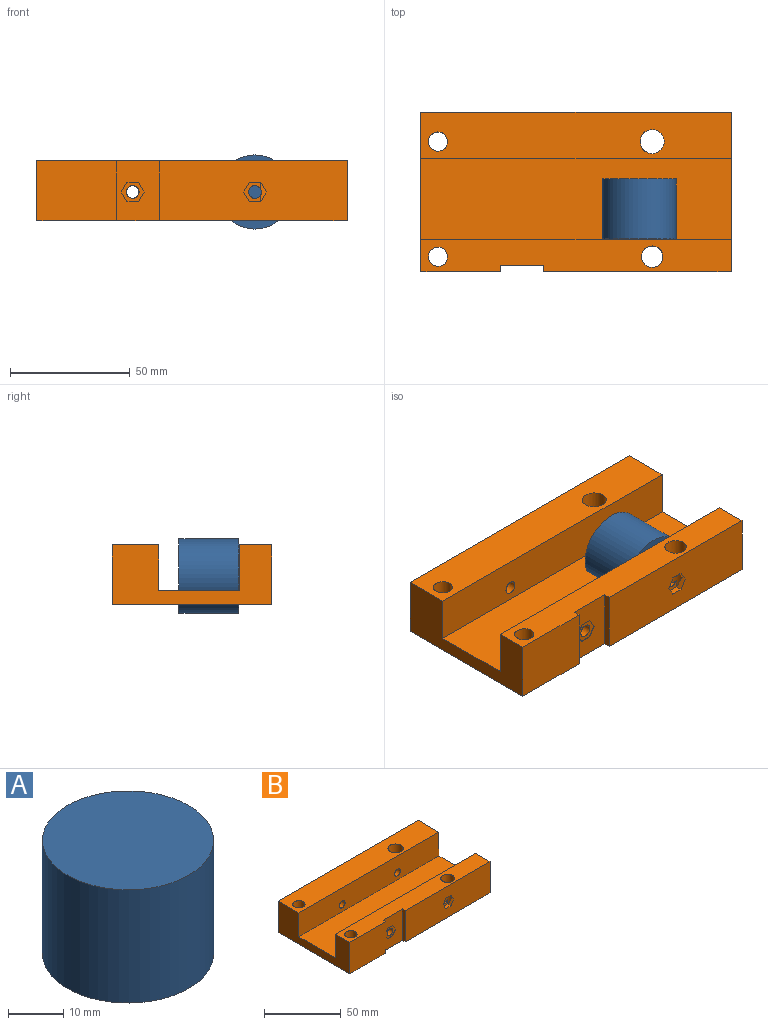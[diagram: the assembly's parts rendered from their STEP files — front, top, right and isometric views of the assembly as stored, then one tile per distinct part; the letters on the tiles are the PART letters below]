
ASSEMBLY  parts=2 mates=1
PART A: 3 faces, bbox 30.9x30.9x25 mm
  f0: cylinder r=15.45mm len=30.9mm, axis (0,0,-1), area 2426.6mm2, adj f1,f2
  f1: plane 30.9x30.9mm, normal (0,0,1), area 749.7mm2, adj f0
  f2: plane 30.9x30.9mm, normal (0,0,-1), area 749.7mm2, adj f0
PART B: 36 faces, bbox 129.2x66.4x25 mm
  f0: cylinder r=2.65mm len=10.43mm, axis (0,-1,0), area 138.4mm2, adj f1,f16,f35
  f1: plane 8.31x7.22mm, normal (0,-1,0), area 28.3mm2, adj f0,f21,f22,f23,f24,f25,f26,f35
  f2: cylinder r=5mm len=25mm, axis (0,0,-1), area 742.5mm2, adj f8,f9,f10
  f3: plane 129.24x25mm, normal (0,1,0), area 3187mm2, adj f4,f7,f8,f9,f10,f11
  f4: plane 66.44x25mm, normal (-1,0,0), area 1019.3mm2, adj f3,f5,f8,f9,f16,f17,f20,f34
  f5: plane 129.24x19mm, normal (0,-1,0), area 2411.5mm2, adj f4,f7,f8,f10,f11,f34
  f6: cylinder r=4mm len=25mm, axis (0,0,-1), area 628.3mm2, adj f8,f9
  f7: plane 66.44x25mm, normal (1,0,0), area 1019.3mm2, adj f3,f5,f8,f9,f14,f16,f20,f34
  f8: plane 129.24x19.33mm, normal (0,0,1), area 2369.9mm2, adj f2,f3,f4,f5,f6,f7
  f9: plane 129.24x66.44mm, normal (0,0,-1), area 8297.5mm2, adj f2,f3,f4,f6,f7,f12,f14,f15
  f10: cylinder r=2.65mm len=19.33mm, axis (0,-1,0), area 273.2mm2, adj f2,f3,f5
  f11: cylinder r=2.65mm len=19.33mm, axis (0,-1,0), area 321.9mm2, adj f3,f5
  f12: plane 25x17.78mm, normal (0,-1,0), area 384.6mm2, adj f9,f15,f18,f20,f27,f28,f29,f30
  f13: cylinder r=2.65mm len=10.33mm, axis (0,-1,0), area 172.1mm2, adj f16,f33
  f14: plane 78.22x25mm, normal (0,-1,0), area 1895.7mm2, adj f7,f9,f15,f20,f21,f22,f23,f24
  f15: plane 25x2.67mm, normal (-1,0,0), area 66.7mm2, adj f9,f12,f14,f20
  f16: plane 129.24x19mm, normal (0,1,0), area 2411.5mm2, adj f0,f4,f7,f13,f20,f34
  f17: plane 33.24x25mm, normal (0,-1,0), area 831.1mm2, adj f4,f9,f18,f20
  f18: plane 25x2.67mm, normal (1,0,0), area 66.7mm2, adj f9,f12,f17,f20
  f19: cylinder r=4mm len=25mm, axis (0,0,-1), area 628.3mm2, adj f9,f20
  f20: plane 129.24x13.33mm, normal (0,0,1), area 1562mm2, adj f4,f7,f12,f14,f15,f16,f17,f18
  f21: plane 4.8x2.9mm, normal (0,0,-1), area 13.9mm2, adj f1,f14,f22,f26
  f22: plane 4.16x2.9mm, normal (0.87,0,-0.5), area 13.9mm2, adj f1,f14,f21,f23
  f23: plane 4.16x2.9mm, normal (0.87,0,0.5), area 13.9mm2, adj f1,f14,f22,f24
  f24: plane 4.8x2.9mm, normal (0,0,1), area 13.9mm2, adj f1,f14,f23,f25
  f25: plane 4.16x2.9mm, normal (-0.87,0,0.5), area 10.5mm2, adj f1,f14,f24,f26,f35
  f26: plane 4.16x2.9mm, normal (-0.87,0,-0.5), area 10.5mm2, adj f1,f14,f21,f25,f35
  f27: plane 4.8x0.33mm, normal (0,0,-1), area 1.6mm2, adj f12,f28,f32,f33
  f28: plane 4.16x2.4mm, normal (0.87,0,-0.5), area 1.6mm2, adj f12,f27,f29,f33
  f29: plane 4.16x2.4mm, normal (0.87,0,0.5), area 1.6mm2, adj f12,f28,f30,f33
  f30: plane 4.8x0.33mm, normal (0,0,1), area 1.6mm2, adj f12,f29,f31,f33
  f31: plane 4.16x2.4mm, normal (-0.87,0,0.5), area 1.6mm2, adj f12,f30,f32,f33
  f32: plane 4.16x2.4mm, normal (-0.87,0,-0.5), area 1.6mm2, adj f12,f27,f31,f33
  f33: plane 9.6x8.31mm, normal (0,-1,0), area 37.8mm2, adj f13,f27,f28,f29,f30,f31,f32
  f34: plane 129.24x33.78mm, normal (0,0,1), area 4365.6mm2, adj f4,f5,f7,f16
  f35: cylinder r=4.5mm len=25mm, axis (0,0,-1), area 663mm2, adj f0,f1,f9,f20,f25,f26
PLACE A rot(axis=(-1,0,0),90deg) t=(43.88,-0.55,120.23)mm
PLACE B t=(77.68,12.2,66.54)mm
MATE cylindrical A.f0 <-> B.f0  axis (0,-1,0) through (110.49,-0.55,78.54)mm
